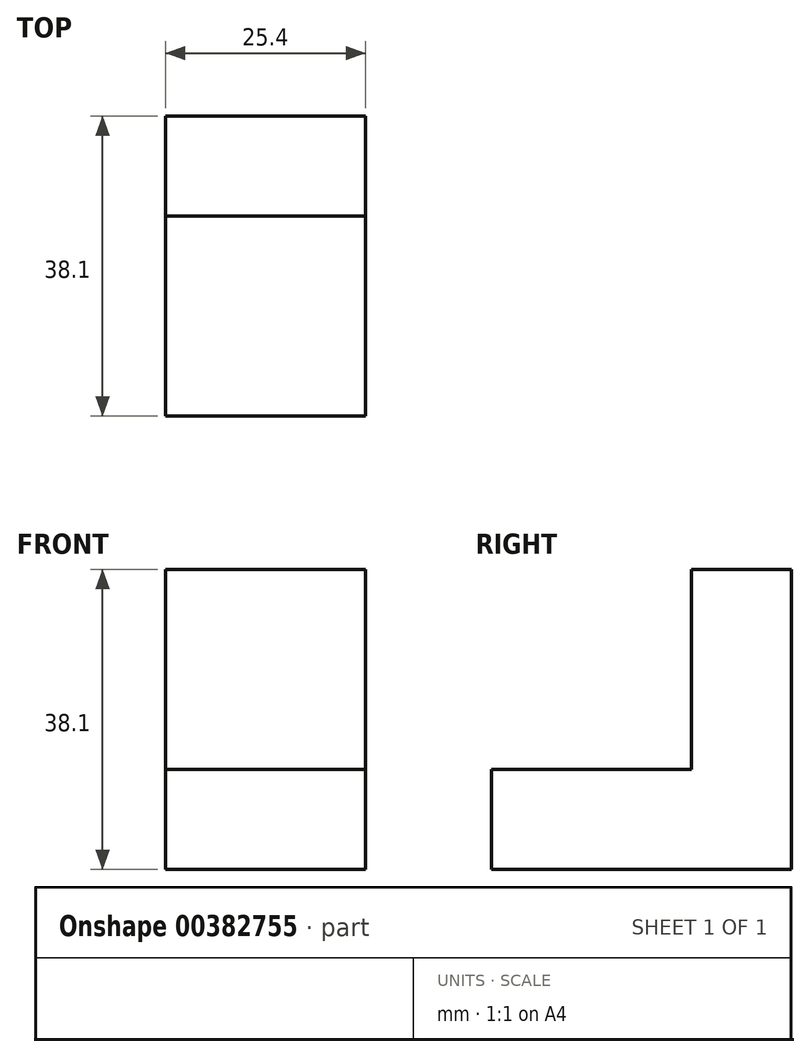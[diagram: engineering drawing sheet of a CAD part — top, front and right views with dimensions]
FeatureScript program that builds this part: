
annotation { "Feature Type Name" : "Feature", "Feature Type Description" : "" }
export const myFeature = defineFeature(function(context is Context, id is Id, definition is map)
    precondition{}
    {
        {
            var Q0;
            Q0=qCreatedBy(makeId("Right.planeOp"),FACE);
            var sketch = newSketch(context, id + "F0", { "sketchPlane" : qUnion([Q0])});
            skLineSegment(sketch, "E0", {"start": v(0, 0) * mm, "end": v(38.1, 0) * mm});
            skLineSegment(sketch, "E1", {"start": v(38.1, 0) * mm, "end": v(38.1, 38.1) * mm});
            skLineSegment(sketch, "E2", {"start": v(38.1, 38.1) * mm, "end": v(25.4, 38.1) * mm});
            skLineSegment(sketch, "E3", {"start": v(25.4, 38.1) * mm, "end": v(25.4, 12.7) * mm});
            skLineSegment(sketch, "E4", {"start": v(25.4, 12.7) * mm, "end": v(0, 12.7) * mm});
            skLineSegment(sketch, "E5", {"start": v(0, 12.7) * mm, "end": v(0, 0) * mm});
            skSolve(sketch);
        }
        {
            var Q0;
            Q0 = qSketchRegion(id + "F0", true);
            extrude(context, id + "F1", {"entities" : qUnion([Q0]), "depth" : 25.4 * mm});
        }
    });
